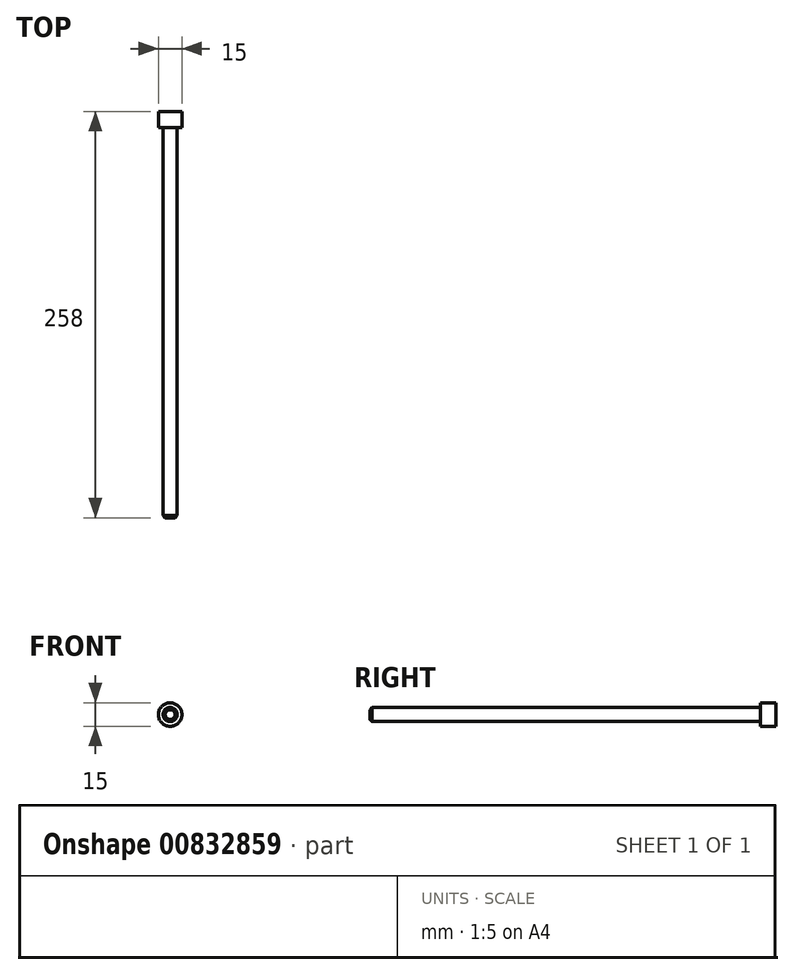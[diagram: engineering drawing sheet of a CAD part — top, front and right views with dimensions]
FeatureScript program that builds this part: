
annotation { "Feature Type Name" : "Feature", "Feature Type Description" : "" }
export const myFeature = defineFeature(function(context is Context, id is Id, definition is map)
    precondition{}
    {
        {
            var Q0;
            Q0=qCreatedBy(makeId("Front.planeOp"),FACE);
            var sketch = newSketch(context, id + "F0", { "sketchPlane" : qUnion([Q0])});
            skCircle(sketch, "E0", {"center": v(0, 0) * mm, "radius": 4.5 * mm});
            skSolve(sketch);
        }
        {
            var Q0;
            Q0 = qSketchRegion(id + "F0", true);
            extrude(context, id + "F1", {"entities" : qUnion([Q0]), "depth" : 248 * mm, "offsetDistance" : 25 * mm});
        }
        {
            var Q0;
            Q0=makeQuery(id+"F1.opExtrude","CAP_FACE",FACE,{"disambiguationData":[OSD([sQuery(id+"F0.wireOp",EDGE,"E0")])],"isStart":true});
            var sketch = newSketch(context, id + "F2", { "sketchPlane" : qUnion([Q0])});
            skCircle(sketch, "E1", {"center": v(0, 0) * mm, "radius": 7.5 * mm});
            skSolve(sketch);
        }
        {
            var Q0;
            Q0 = qSketchRegion(id + "F2", true);
            extrude(context, id + "F3", {"entities" : qUnion([Q0]), "operationType" : NewBodyOperationType.ADD, "depth" : 10 * mm, "offsetDistance" : 25 * mm});
        }
        {
            var Q0;
            Q0=makeQuery(id+"F1.opExtrude","CAP_EDGE",EDGE,{"disambiguationData":[OSD([sQuery(id+"F0.wireOp",EDGE,"E0")])],"isStart":false});
            chamfer(context, id + "F4", {"entities" : qUnion([Q0]), "width" : 1.4 * mm, "tangentPropagation" : true});
        }
    });
